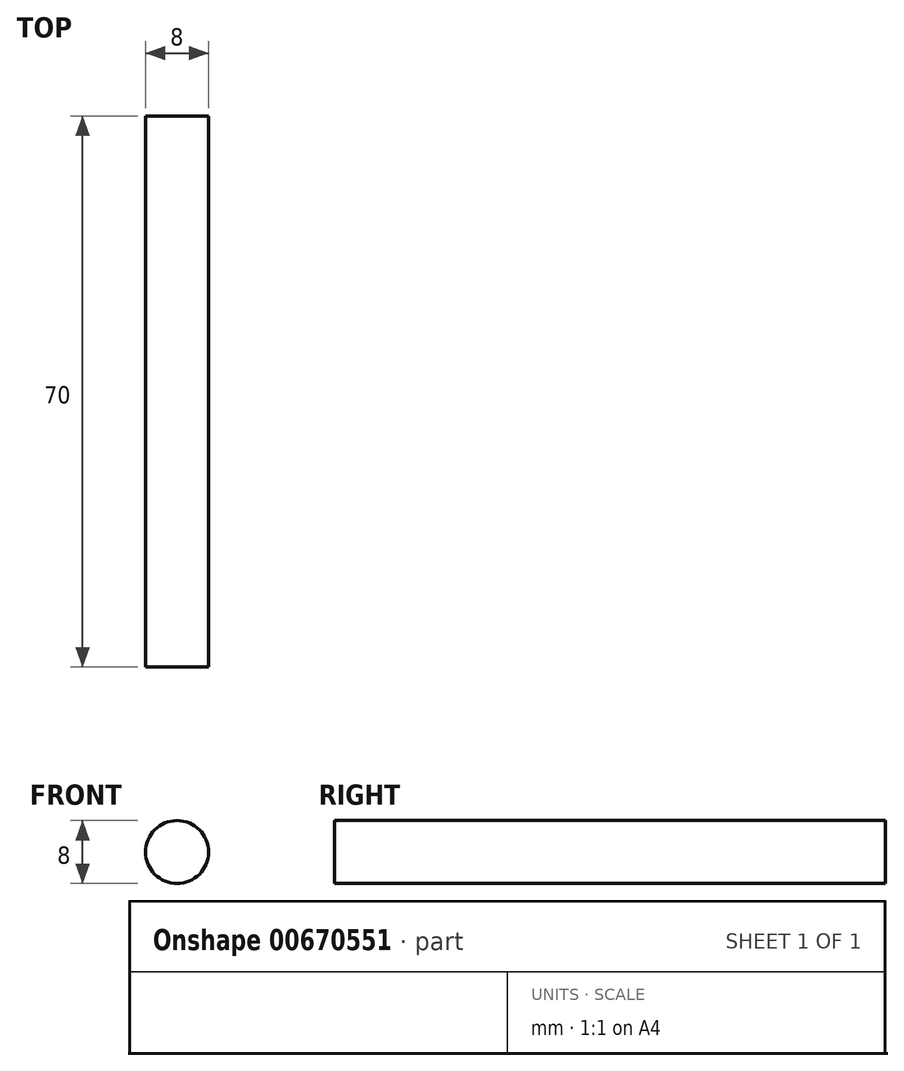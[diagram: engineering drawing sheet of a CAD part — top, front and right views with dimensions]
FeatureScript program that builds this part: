
annotation { "Feature Type Name" : "Feature", "Feature Type Description" : "" }
export const myFeature = defineFeature(function(context is Context, id is Id, definition is map)
    precondition{}
    {
        {
            var Q0;
            Q0=qCreatedBy(makeId("Front.planeOp"),FACE);
            var sketch = newSketch(context, id + "F0", { "sketchPlane" : qUnion([Q0])});
            skCircle(sketch, "E0", {"center": v(0, 0) * mm, "radius": 4 * mm});
            skSolve(sketch);
        }
        {
            var Q0;
            Q0=makeQuery(id+"F0.imprint","IMPRINT",FACE,{"disambiguationData":[TD([[makeQuery(id+"F0.imprint","IMPRINT",EDGE,{"derivedFrom":sQuery(id+"F0.wireOp",EDGE,"E0")}),1.0]])]});
            var Q1;
            Q1=sQuery(id+"F0.wireOp",EDGE,"E0");
            extrude(context, id + "F1", {"entities" : qUnion([Q0]), "surfaceEntities" : qUnion([Q1]), "depth" : 70 * mm, "offsetDistance" : 25 * mm});
        }
    });
